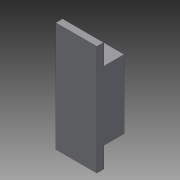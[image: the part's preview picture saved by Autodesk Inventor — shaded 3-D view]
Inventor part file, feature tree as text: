
AUTODESK INVENTOR PART (.ipt)
format: ipt  version: 2015 SP1 (Build 190203100, 203)  size: 107,008 bytes
history: native  units: mm
features: extrude x3, sketch x3
ambient origin geometry x8: Origin, YZ Plane, XZ Plane, XY Plane, X Axis, Y Axis, Z Axis, Center Point
bodies: Solid1 (feature_tree)
feature tree (6):
  extrude  "Extrusion1"  Depth=80.0mm
  extrude  "Extrusion2"  Depth=15.0mm
  extrude  "Extrusion4"  Depth=15.0mm TaperAngle=0.0deg
  sketch  "Sketch1"  dims[d0=30.0mm d1=80.0mm]
  sketch  "Sketch2"  dims[d2=5.0mm d3=0.0mm d4=15.0mm]
  sketch  "Sketch3"  dims[d5=15.0mm d6=15.0mm d7=0.0mm d8=50.0mm d9=24.5mm d10=12.5mm d11=15.0mm d14=8.0mm d15=0.0mm]
